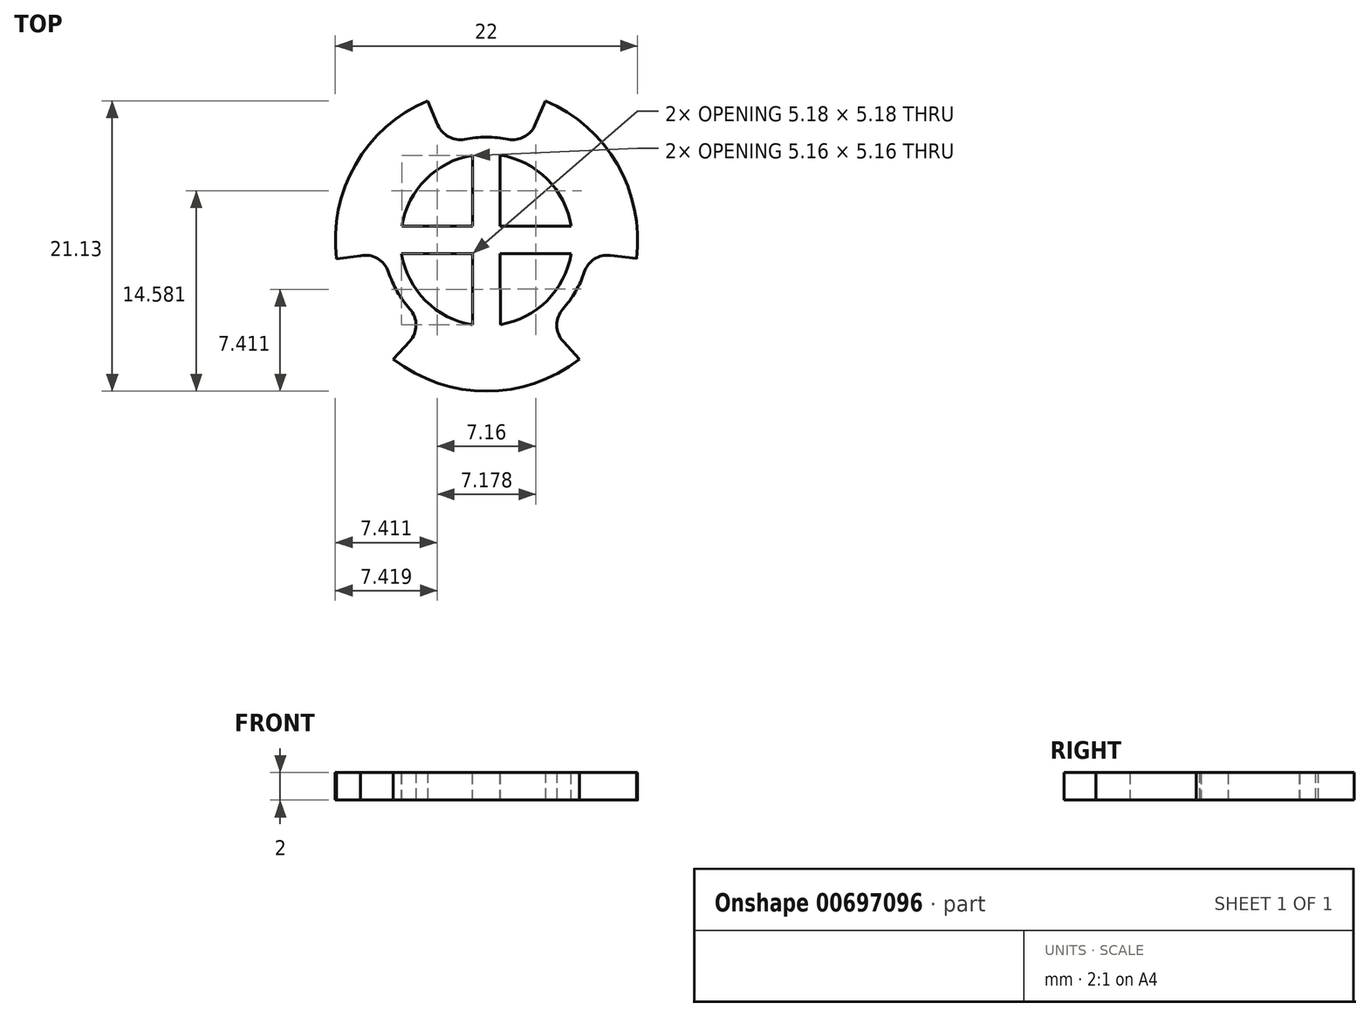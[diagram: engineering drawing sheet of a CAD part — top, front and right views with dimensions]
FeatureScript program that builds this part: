
annotation { "Feature Type Name" : "Feature", "Feature Type Description" : "" }
export const myFeature = defineFeature(function(context is Context, id is Id, definition is map)
    precondition{}
    {
        {
            var Q0;
            Q0=qCreatedBy(makeId("Top.planeOp"),FACE);
            var sketch = newSketch(context, id + "F0", { "sketchPlane" : qUnion([Q0])});
            skLineSegment(sketch, "E0", {"start": v(0, 0) * mm, "end": v(0, 9.25) * mm, "construction": true});
            skLineSegment(sketch, "E1", {"start": v(0, 0) * mm, "end": v(8.01, -4.62) * mm, "construction": true});
            skLineSegment(sketch, "E2", {"start": v(0, 0) * mm, "end": v(-8.01, -4.62) * mm, "construction": true});
            skLineSegment(sketch, "E3", {"start": v(0, 0) * mm, "end": v(1.92, 9.05) * mm, "construction": true});
            skLineSegment(sketch, "E4", {"start": v(0, 0) * mm, "end": v(-1.92, 9.05) * mm, "construction": true});
            skLineSegment(sketch, "E5", {"start": v(0, 0) * mm, "end": v(8.8, -2.86) * mm, "construction": true});
            skLineSegment(sketch, "E6", {"start": v(0, 0) * mm, "end": v(6.87, -6.19) * mm, "construction": true});
            skLineSegment(sketch, "E7", {"start": v(0, 0) * mm, "end": v(-6.87, -6.19) * mm, "construction": true});
            skLineSegment(sketch, "E8", {"start": v(0, 0) * mm, "end": v(-8.8, -2.86) * mm, "construction": true});
            skArc(sketch, "E9", {"start": v(1.92, 9.05) * mm, "mid": v(0, 9.23) * mm, "end": v(-1.92, 9.05) * mm});
            skArc(sketch, "E10", {"start": v(-8.8, -2.86) * mm, "mid": v(-8.01, -4.62) * mm, "end": v(-6.87, -6.19) * mm});
            skArc(sketch, "E11", {"start": v(6.87, -6.19) * mm, "mid": v(8.01, -4.62) * mm, "end": v(8.8, -2.86) * mm});
            skArc(sketch, "E12.0.startCap", {"start": v(2.26, 10.77) * mm, "mid": v(3.64, 8.71) * mm, "end": v(1.59, 7.33) * mm});
            skArc(sketch, "E12.0.endCap", {"start": v(-1.59, 7.33) * mm, "mid": v(-3.64, 8.71) * mm, "end": v(-2.26, 10.77) * mm});
            skArc(sketch, "E12.0.left", {"start": v(1.59, 7.33) * mm, "mid": v(0, 7.48) * mm, "end": v(-1.59, 7.33) * mm});
            skArc(sketch, "E12.0.right", {"start": v(2.26, 10.77) * mm, "mid": v(0, 10.98) * mm, "end": v(-2.26, 10.77) * mm});
            skArc(sketch, "E13.0.startCap", {"start": v(8.17, -7.36) * mm, "mid": v(5.7, -7.49) * mm, "end": v(5.57, -5.02) * mm});
            skArc(sketch, "E13.0.endCap", {"start": v(7.13, -2.32) * mm, "mid": v(9.34, -1.2) * mm, "end": v(10.46, -3.4) * mm});
            skArc(sketch, "E13.0.left", {"start": v(5.57, -5.02) * mm, "mid": v(6.5, -3.75) * mm, "end": v(7.13, -2.32) * mm});
            skArc(sketch, "E13.0.right", {"start": v(8.17, -7.36) * mm, "mid": v(9.53, -5.5) * mm, "end": v(10.46, -3.4) * mm});
            skArc(sketch, "E13.1.startCap", {"start": v(-10.46, -3.4) * mm, "mid": v(-9.34, -1.2) * mm, "end": v(-7.13, -2.32) * mm});
            skArc(sketch, "E13.1.endCap", {"start": v(-5.57, -5.02) * mm, "mid": v(-5.7, -7.49) * mm, "end": v(-8.17, -7.36) * mm});
            skArc(sketch, "E13.1.left", {"start": v(-7.13, -2.32) * mm, "mid": v(-6.5, -3.75) * mm, "end": v(-5.57, -5.02) * mm});
            skArc(sketch, "E13.1.right", {"start": v(-10.46, -3.4) * mm, "mid": v(-9.53, -5.5) * mm, "end": v(-8.17, -7.36) * mm});
            skCircle(sketch, "E14", {"center": v(0, 0) * mm, "radius": 11 * mm});
            skLineSegment(sketch, "E15", {"start": v(0, 0) * mm, "end": v(-3.54, 8.37) * mm, "construction": true});
            skLineSegment(sketch, "E16", {"start": v(0, 0) * mm, "end": v(3.54, 8.37) * mm, "construction": true});
            skLineSegment(sketch, "E17", {"start": v(0, 0) * mm, "end": v(9.01, -1.12) * mm, "construction": true});
            skLineSegment(sketch, "E18", {"start": v(0, 0) * mm, "end": v(5.59, -7.37) * mm, "construction": true});
            skLineSegment(sketch, "E19", {"start": v(0, 0) * mm, "end": v(-5.59, -7.37) * mm, "construction": true});
            skLineSegment(sketch, "E20", {"start": v(0, 0) * mm, "end": v(-9.18, -1.15) * mm, "construction": true});
            skLineSegment(sketch, "E21", {"start": v(5.59, -7.37) * mm, "end": v(6.77, -8.67) * mm});
            skLineSegment(sketch, "E22", {"start": v(-5.59, -7.37) * mm, "end": v(-6.77, -8.67) * mm});
            skLineSegment(sketch, "E23", {"start": v(9.01, -1.12) * mm, "end": v(10.92, -1.36) * mm});
            skLineSegment(sketch, "E24", {"start": v(3.54, 8.37) * mm, "end": v(4.28, 10.13) * mm});
            skLineSegment(sketch, "E25", {"start": v(-3.54, 8.37) * mm, "end": v(-4.28, 10.13) * mm});
            skLineSegment(sketch, "E26", {"start": v(-9.18, -1.15) * mm, "end": v(-10.91, -1.37) * mm});
            skSolve(sketch);
        }
        {
            var Q0;
            {var subQ10=sQuery(id+"F0.wireOp",EDGE,"E12.0.left");Q0=makeQuery(id+"F0.imprint","IMPRINT",FACE,{"disambiguationData":[TD([[makeQuery(id+"F0.imprint","IMPRINT",EDGE,{"derivedFrom":subQ10}),1.0]])]});}
            extrude(context, id + "F1", {"entities" : qUnion([Q0]), "depth" : 2 * mm, "offsetDistance" : 25 * mm});
        }
        {
            var Q0;
            Q0=makeQuery(id+"F1.opExtrude","CAP_FACE",FACE,{"disambiguationData":[OSD([sQuery(id+"F0.wireOp",EDGE,"E12.0.startCap"),sQuery(id+"F0.wireOp",EDGE,"E12.0.endCap"),sQuery(id+"F0.wireOp",EDGE,"E12.0.left"),sQuery(id+"F0.wireOp",EDGE,"E13.0.startCap"),sQuery(id+"F0.wireOp",EDGE,"E13.0.endCap"),sQuery(id+"F0.wireOp",EDGE,"E13.0.left"),sQuery(id+"F0.wireOp",EDGE,"E13.1.startCap"),sQuery(id+"F0.wireOp",EDGE,"E13.1.endCap"),sQuery(id+"F0.wireOp",EDGE,"E13.1.left"),sQuery(id+"F0.wireOp",EDGE,"E14"),sQuery(id+"F0.wireOp",EDGE,"E21"),sQuery(id+"F0.wireOp",EDGE,"E22"),sQuery(id+"F0.wireOp",EDGE,"E23"),sQuery(id+"F0.wireOp",EDGE,"E24"),sQuery(id+"F0.wireOp",EDGE,"E25"),sQuery(id+"F0.wireOp",EDGE,"E26")])],"isStart":false});
            var sketch = newSketch(context, id + "F2", { "sketchPlane" : qUnion([Q0])});
            skCircle(sketch, "E27", {"center": v(0, 0) * mm, "radius": 7.5 * mm});
            skLineSegment(sketch, "E28", {"start": v(0, 6.5) * mm, "end": v(0, -6.5) * mm, "construction": true});
            skLineSegment(sketch, "E29", {"start": v(-6.5, 0) * mm, "end": v(6.5, 0) * mm, "construction": true});
            skLineSegment(sketch, "E30", {"start": v(-1, 6.16) * mm, "end": v(-1, 1) * mm});
            skLineSegment(sketch, "E31", {"start": v(-6.18, -1) * mm, "end": v(-1, -1) * mm});
            skLineSegment(sketch, "E32", {"start": v(-1, -1) * mm, "end": v(-1, -6.18) * mm});
            skLineSegment(sketch, "E33", {"start": v(1, 6.18) * mm, "end": v(1, 1) * mm});
            skLineSegment(sketch, "E34", {"start": v(1, 1) * mm, "end": v(6.18, 1) * mm});
            skLineSegment(sketch, "E35", {"start": v(6.16, -1) * mm, "end": v(1, -1) * mm});
            skLineSegment(sketch, "E36", {"start": v(1, -1) * mm, "end": v(1, -6.16) * mm});
            skLineSegment(sketch, "E37", {"start": v(-1, 1) * mm, "end": v(-6.16, 1) * mm});
            skArc(sketch, "E38", {"start": v(-1, 6.16) * mm, "mid": v(-4.41, 4.41) * mm, "end": v(-6.16, 1) * mm});
            skArc(sketch, "E39", {"start": v(1, 6.18) * mm, "mid": v(4.43, 4.43) * mm, "end": v(6.18, 1) * mm});
            skArc(sketch, "E40", {"start": v(6.16, -1) * mm, "mid": v(4.42, -4.4) * mm, "end": v(1, -6.16) * mm});
            skArc(sketch, "E41", {"start": v(-1, -6.18) * mm, "mid": v(-4.42, -4.42) * mm, "end": v(-6.18, -1) * mm});
            skCircle(sketch, "E42", {"center": v(0, 0) * mm, "radius": 6.25 * mm, "construction": true});
            skSolve(sketch);
        }
        {
            var Q0;
            {var subQ0=sQuery(id+"F2.wireOp",EDGE,"E27");var subQ1=makeQuery(id+"F1.opExtrude","CAP_EDGE",EDGE,{"disambiguationData":[OSD([sQuery(id+"F0.wireOp",EDGE,"E12.0.left")])],"isStart":false});var subQ2=makeQuery(id+"F2.imprint","INTERSECT",VERTEX,{"disambiguationData":[OD(0.0)],"derivedFrom":[subQ1,subQ0]});Q0=makeQuery(id+"F2.imprint","IMPRINT",FACE,{"disambiguationData":[TD([[makeQuery(id+"F2.imprint","IMPRINT",EDGE,{"disambiguationData":[TD([[subQ2,1.0]])],"derivedFrom":subQ0}),1.0]])]});}
            var Q1;
            Q1=makeQuery(id+"F2.imprint","IMPRINT",FACE,{"disambiguationData":[TD([[makeQuery(id+"F2.imprint","IMPRINT",EDGE,{"derivedFrom":sQuery(id+"F2.wireOp",EDGE,"E30")}),-1.0]])]});
            var Q2;
            Q2=makeQuery(id+"F2.imprint","IMPRINT",FACE,{"disambiguationData":[TD([[makeQuery(id+"F2.imprint","IMPRINT",EDGE,{"derivedFrom":sQuery(id+"F2.wireOp",EDGE,"E33")}),1.0]])]});
            var Q3;
            Q3=makeQuery(id+"F2.imprint","IMPRINT",FACE,{"disambiguationData":[TD([[makeQuery(id+"F2.imprint","IMPRINT",EDGE,{"derivedFrom":sQuery(id+"F2.wireOp",EDGE,"E35")}),1.0]])]});
            var Q4;
            Q4=makeQuery(id+"F2.imprint","IMPRINT",FACE,{"disambiguationData":[TD([[makeQuery(id+"F2.imprint","IMPRINT",EDGE,{"derivedFrom":sQuery(id+"F2.wireOp",EDGE,"E31")}),-1.0]])]});
            extrude(context, id + "F3", {"entities" : qUnion([Q0, Q1, Q2, Q3, Q4]), "operationType" : NewBodyOperationType.REMOVE, "oppositeDirection" : true, "depth" : 25 * mm, "offsetDistance" : 25 * mm});
        }
    });
